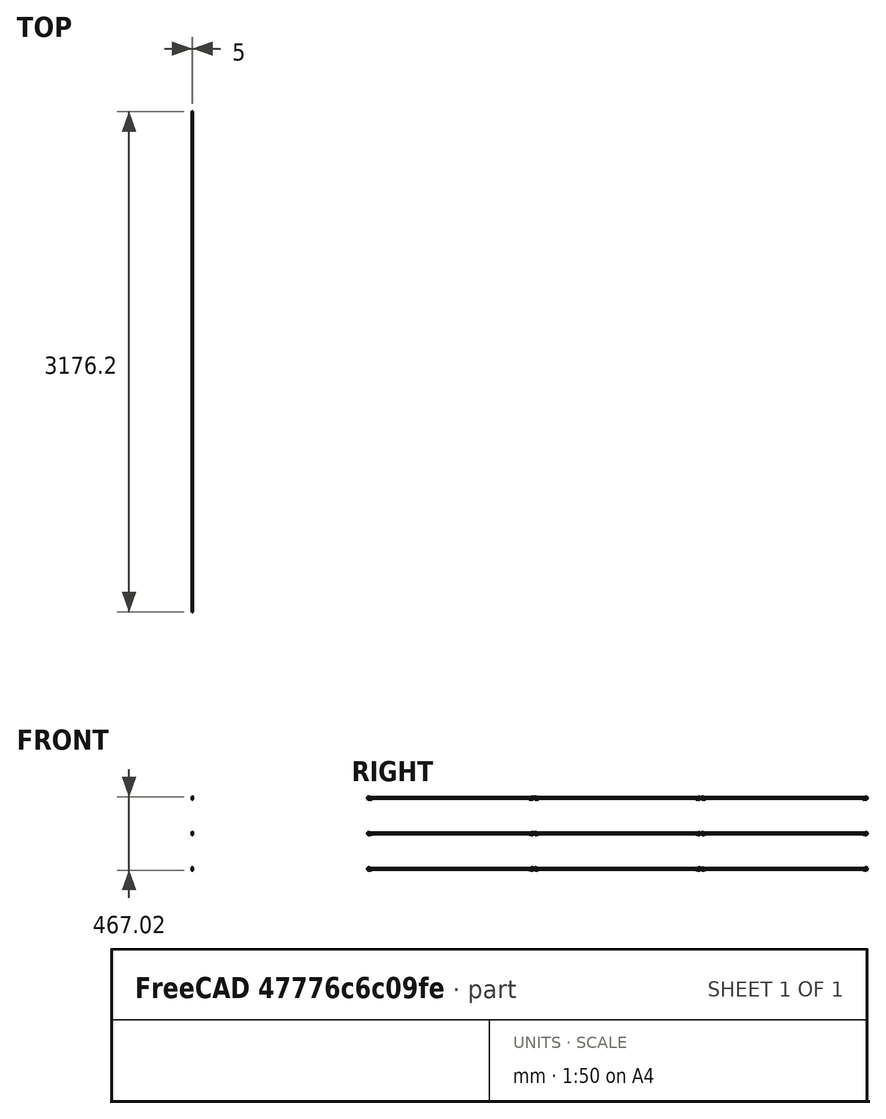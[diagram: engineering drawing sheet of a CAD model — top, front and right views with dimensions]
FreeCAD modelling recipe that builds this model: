
FCSTD DOCUMENT  (FreeCAD 0.17R11051 (Git))
Label: loft_ropes
License: All rights reserved
LicenseURL: http://en.wikipedia.org/wiki/All_rights_reserved
objects: Sketcher::SketchObject×3, Part::FeaturePython×2, Part::Sweep×1, Part::Extrusion×1, Part::Compound×1, App::DocumentObjectGroup×1
note: 8 computed .brp shape members not serialized (recipe doc carries the construction recipe); baked Part::Feature solids carry a one-line shape summary decoded from their .brp

FEATURE [Sketcher::SketchObject] Sketch001
  Placement = pos=(20,0,0) rot=(0,-1,0;1.5708rad)
  sketch-geometry (1):
    g0: Circle CenterX=5 CenterY=0 CenterZ=0 NormalX=0 NormalY=0 NormalZ=1 Radius=2.5
  constraints (3):
    c: PointOnObject(g0,g-1)
    c: DistanceX(g-1,g0) = 5
    c: Radius(g0) = 2.5
FEATURE [Sketcher::SketchObject] Sketch
  Placement = pos=(20,0,0) rot=(0,-1,0;1.5708rad)
  sketch-geometry (1):
    g0: Circle CenterX=0 CenterY=0 CenterZ=0 NormalX=0 NormalY=0 NormalZ=1 Radius=2.5
  constraints (2):
    c: Radius(g0) = 2.5
    c: Coincident(g0,g-1)
FEATURE [Sketcher::SketchObject] Sketch002
  Placement = pos=(20,0,0) rot=(0.57735,-0.57735,0.57735;2.0944rad)
  sketch-geometry (43):
    g0: LineSegment [constr] StartX=3.375 StartY=25.8457 StartZ=0 EndX=-3.375 EndY=25.8457 EndZ=0
    g1: LineSegment [constr] StartX=-3.375 StartY=25.8457 StartZ=0 EndX=-6.75 EndY=20 EndZ=0
    g2: LineSegment [constr] StartX=-6.75 StartY=20 StartZ=0 EndX=-3.375 EndY=14.1543 EndZ=0
    g3: LineSegment [constr] StartX=-3.375 StartY=14.1543 StartZ=0 EndX=3.375 EndY=14.1543 EndZ=0
    g4: LineSegment [constr] StartX=3.375 StartY=14.1543 StartZ=0 EndX=6.75 EndY=20 EndZ=0
    g5: LineSegment [constr] StartX=6.75 StartY=20 StartZ=0 EndX=3.375 EndY=25.8457 EndZ=0
    g6: Circle [constr] CenterX=0 CenterY=20 CenterZ=0 NormalX=0 NormalY=0 NormalZ=1 Radius=6.75
    g7: Circle [constr] CenterX=-3.375 CenterY=14.1543 CenterZ=0 NormalX=0 NormalY=0 NormalZ=1 Radius=1
    g8: Circle [constr] CenterX=-6.75 CenterY=20 CenterZ=0 NormalX=0 NormalY=0 NormalZ=1 Radius=1
    g9: Circle [constr] CenterX=-3.375 CenterY=25.8457 CenterZ=0 NormalX=0 NormalY=0 NormalZ=1 Radius=1
    g10: Circle [constr] CenterX=3.375 CenterY=25.8457 CenterZ=0 NormalX=0 NormalY=0 NormalZ=1 Radius=1
    g11: Circle [constr] CenterX=6.75 CenterY=20 CenterZ=0 NormalX=0 NormalY=0 NormalZ=1 Radius=1
    g12: Circle [constr] CenterX=3.375 CenterY=14.1543 CenterZ=0 NormalX=0 NormalY=0 NormalZ=1 Radius=1
    g13: LineSegment StartX=0 StartY=5 StartZ=0 EndX=0 EndY=0 EndZ=0
    g14: LineSegment StartX=5 StartY=5 StartZ=0 EndX=5 EndY=0 EndZ=0
    g15: LineSegment [constr] StartX=0 StartY=5 StartZ=0 EndX=0 EndY=10 EndZ=0
    g16: LineSegment [constr] StartX=5 StartY=5 StartZ=0 EndX=5 EndY=10 EndZ=0
    g17: Circle [constr] CenterX=0 CenterY=10 CenterZ=0 NormalX=0 NormalY=0 NormalZ=1 Radius=3.32889e-07
    g18: Circle [constr] CenterX=-3.375 CenterY=14.1543 CenterZ=0 NormalX=0 NormalY=0 NormalZ=1 Radius=3.32889e-07
    g19: Circle [constr] CenterX=-6.75 CenterY=20 CenterZ=0 NormalX=0 NormalY=0 NormalZ=1 Radius=3.32889e-07
    g20: Circle [constr] CenterX=-3.375 CenterY=25.8457 CenterZ=0 NormalX=0 NormalY=0 NormalZ=1 Radius=3.32889e-07
    g21: Circle [constr] CenterX=3.375 CenterY=25.8457 CenterZ=0 NormalX=0 NormalY=0 NormalZ=1 Radius=3.32889e-07
    g22: Circle [constr] CenterX=6.75 CenterY=20 CenterZ=0 NormalX=0 NormalY=0 NormalZ=1 Radius=3.32889e-07
    g23: Circle [constr] CenterX=5 CenterY=10 CenterZ=0 NormalX=0 NormalY=0 NormalZ=1 Radius=3.32889e-07
    g24-g33: Circle [constr] x10 (B-spline internal-alignment scaffolding for g34; pole/knot coordinates omitted)
    g34: BSplineCurve PolesCount=10 KnotsCount=8 Degree=3 IsPeriodic=0
    g35-g42: GeomPoint [constr] x8 (B-spline internal-alignment scaffolding for g34; pole/knot coordinates omitted)
  constraints (57):
    c: Coincident(g0,g1)
    c: Coincident(g1,g2)
    c: Coincident(g2,g3)
    c: Coincident(g3,g4)
    c: Coincident(g4,g5)
    c: Coincident(g5,g0)
    c: Equal(g0, g1-g5) x5
    c: PointOnObject(g0,g6)
    c: PointOnObject(g1,g6)
    c: PointOnObject(g2,g6)
    c: PointOnObject(g4,g6)
    c: PointOnObject(g5,g6)
    c: Coincident(g7,g2)
    c: Coincident(g8,g1)
    c: Coincident(g9,g0)
    c: Coincident(g10,g0)
    c: Coincident(g11,g4)
    c: Coincident(g12,g3)
    c: DistanceX(g1,g4) = 13.5
    c: Vertical(g13)
    c: Vertical(g14)
    c: Vertical(g15)
    c: Vertical(g16)
    c: Coincident(g17,g15)
    c: Coincident(g18,g2)
    c: Coincident(g19,g1)
    c: Coincident(g20,g0)
    c: Coincident(g21,g0)
    c: Coincident(g22,g4)
    c: Coincident(g23,g16)
    c: Coincident(g15,g13)
    c: Coincident(g14,g16)
    c: Radius(g24) = 1
    c: Equal(g24, g25-g33) x9
    c: InternalAlignment(g24-g33 -> g34) x10
    c: InternalAlignment(g35-g42 -> g34) x8
    c: Coincident(g24,g13)
    c: Coincident(g25,g15)
    c: Coincident(g2,g26)
    c: Coincident(g27,g1)
    c: Coincident(g28,g0)
    c: Coincident(g29,g0)
    c: Coincident(g30,g4)
    c: Coincident(g32,g16)
    c: Coincident(g33,g14)
    c: DistanceY(g16,g16) = 5
    c: DistanceY(g-1,g6) = 20
    c: DistanceX(g37,g40) = 11.726
    c: PointOnObject(g6,g-2)
    c: Parallel(g3,g-1)
    c: DistanceX(g13,g14) = 5
    c: Coincident(g13,g-1)
    c: PointOnObject(g3,g6)
    c: PointOnObject(g14,g-1)
    c: Equal(g13,g14)
    c: Equal(g16,g15)
    c: DistanceY(g14,g14) = 5
FEATURE [Part::Sweep] Sweep
  Frenet = false
  Sections = -> [Sketch001,Sketch]
  Solid = true
  Spine = -> Sketch002 [Edge3,Edge2,Edge1]
  Transition = 1
  expr: Placement.Rotation.Axis.z = 1
FEATURE [Part::FeaturePython] Component  label="Sweep001"  # WARN: FeaturePython — macro-defined, semantics opaque (R4)
  CloneOf = -> Sweep
  HorizontalArea = 0
  MoveWithHost = false
  PerimeterLength = 0
  Placement = pos=(1040,0,0) rot=(0,0,1;3.14159rad)
  Role = 0
  VerticalArea = 0
  expr: Placement.Base.z = 0
FEATURE [Part::Extrusion] Extrude
  Base = -> Sketch
  Dir = (1,0,0)
  DirMode = 0
  FaceMakerClass = Part::FaceMakerBullseye
  LengthFwd = 1000
  LengthRev = 0
  Solid = true
  Symmetric = false
  expr: Dir.x = 1
FEATURE [Part::Compound] Compound
  Links = -> [Sweep,Component,Extrude]
  Placement = pos=(2109.7,-536,2615) rot=(-0.707107,0.707107,0;3.14159rad)
FEATURE [App::DocumentObjectGroup] Group  label="utilities"
  Group = -> [Sketch002]
FEATURE [Part::FeaturePython] Array  # Draft array (typed FeaturePython)
  Angle = 360
  ArrayType = 0
  Axis = (0,0,1)
  Base = -> Compound
  Center = (0,0,0)
  Fuse = false
  IntervalAxis = (0,0,0)
  IntervalX = (0,0,225)
  IntervalY = (0,-1060,0)
  IntervalZ = (0,0,0)
  NumberPolar = 1
  NumberX = 3
  NumberY = 3
  NumberZ = 1
